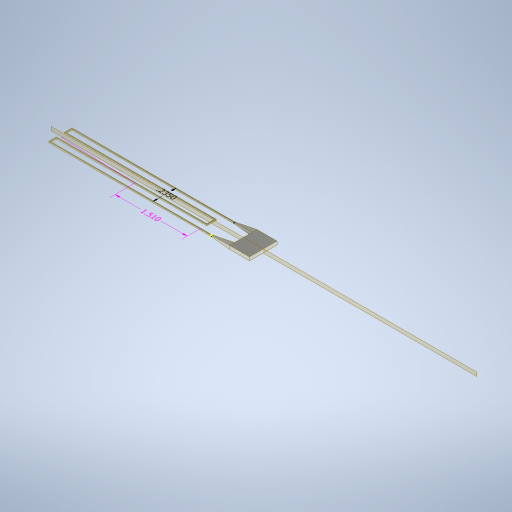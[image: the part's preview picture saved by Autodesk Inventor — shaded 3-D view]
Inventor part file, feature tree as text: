
AUTODESK INVENTOR PART (.ipt)
format: ipt  version: 2024.2 (Build 282272000, 272)  size: 356,352 bytes
history: native  units: in
note: dims shown in document units (in); Inventor stores cm internally (conversion verified against a paired STEP export)
features: sketch x7, other x4, plane x4, extrude x2, sweep x1, loft x1, mirror x1
ambient origin geometry x8: Origin, YZ Plane, XZ Plane, XY Plane, X Axis, Y Axis, Z Axis, Center Point
bodies: Solid1 (feature_tree)
feature tree (20):
  other  "Annotations"
  sweep  "Sweep1"
  plane  "Work Plane1"
  plane  "Work Plane2"
  sketch  "Sketch10"  dims[d24=0.01in d63=0.01in]
  extrude  "Extrusion7"  Depth=0.25in
  plane  "Work Plane3"
  sketch  "Sketch12"  dims[d67=0.08in]
  sketch  "Sketch13"  dims[d69=1.625in]
  loft  "Loft2"
  plane  "Work Plane4"
  mirror  "Mirror2"
  extrude  "Extrusion8"  Depth=0.08in
  sketch  "Sketch1"  dims[d4=0.05in d5=0.05in]
  sketch  "Sketch2"  dims[d6=0.0in d7=0.0in d11=0.25in d19=-0.25in]
  sketch  "Sketch11"  dims[d65=0.075in d66=0.08in]
  other  "Edges3"
  sketch  "Sketch14"  dims[d70=1.625in d71=1.0in d72=0.5in d73=0.0in d74=0.0in d75=0.2in d76=0.05in d77=0.0in d78=0.035in d79=0.0in d80=90.0deg d81=0.0in d82=90.0deg d86=-0.1175in d87=0.2in d88=0.0in d42=0.2341in d43=0.169in d44=0.235in d48=0.2141in d49=0.2512in d50=1.51in]
  other  "Linear Dimension 1"
  other  "Linear Dimension 3"
